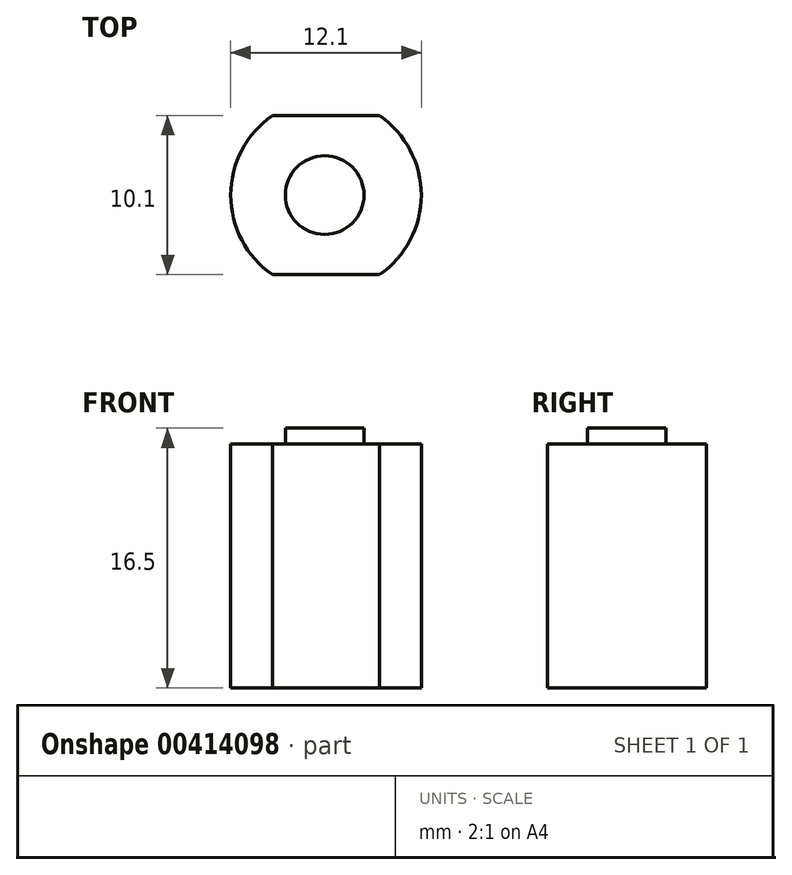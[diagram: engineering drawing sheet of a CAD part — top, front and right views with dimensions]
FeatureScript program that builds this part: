
annotation { "Feature Type Name" : "Feature", "Feature Type Description" : "" }
export const myFeature = defineFeature(function(context is Context, id is Id, definition is map)
    precondition{}
    {
        {
            var Q0;
            Q0=qCreatedBy(makeId("Top.planeOp"),FACE);
            var sketch = newSketch(context, id + "F0", { "sketchPlane" : qUnion([Q0])});
            skLineSegment(sketch, "E0.bottom", {"start": v(3.4, 5.05) * mm, "end": v(-3.4, 5.05) * mm});
            skLineSegment(sketch, "E0.top", {"start": v(3.4, -5.05) * mm, "end": v(-3.4, -5.05) * mm});
            skPoint(sketch, "E0.middle", {"position": v(0, 0) * mm});
            skPoint(sketch, "E1", {"position": v(6.05, 0) * mm});
            skPoint(sketch, "E2", {"position": v(-6.05, 0) * mm});
            skArc(sketch, "E3", {"start": v(3.4, -5.05) * mm, "mid": v(6.05, 0) * mm, "end": v(3.4, 5.05) * mm});
            skArc(sketch, "E4", {"start": v(-3.4, 5.05) * mm, "mid": v(-6.05, 0) * mm, "end": v(-3.4, -5.05) * mm});
            skPoint(sketch, "E5.orphan", {"position": v(6.05, 5.05) * mm});
            skPoint(sketch, "E0.left.end.orphan", {"position": v(6.05, -5.05) * mm});
            skPoint(sketch, "E6.orphan", {"position": v(-6.05, -5.05) * mm});
            skPoint(sketch, "E7.orphan", {"position": v(-6.05, 5.05) * mm});
            skSolve(sketch);
        }
        {
            var Q0;
            Q0=makeQuery(id+"F0.imprint","IMPRINT",FACE,{"disambiguationData":[TD([[makeQuery(id+"F0.imprint","IMPRINT",EDGE,{"derivedFrom":sQuery(id+"F0.wireOp",EDGE,"E0.bottom")}),1.0]])]});
            extrude(context, id + "F1", {"entities" : qUnion([Q0]), "depth" : 15.5 * mm});
        }
        {
            var Q0;
            Q0=makeQuery(id+"F1.opExtrude","CAP_FACE",FACE,{"disambiguationData":[OSD([sQuery(id+"F0.wireOp",EDGE,"E0.bottom"),sQuery(id+"F0.wireOp",EDGE,"E0.top"),sQuery(id+"F0.wireOp",EDGE,"E3"),sQuery(id+"F0.wireOp",EDGE,"E4")])],"isStart":false});
            var sketch = newSketch(context, id + "F2", { "sketchPlane" : qUnion([Q0])});
            skCircle(sketch, "E8", {"center": v(-0.09, 0) * mm, "radius": 2.5 * mm});
            skLineSegment(sketch, "E9.trimOffspring", {"start": v(-0.09, 0) * mm, "end": v(0, 0) * mm});
            skPoint(sketch, "E10.trimOffspring.end.orphan", {"position": v(0, -5.05) * mm});
            skPoint(sketch, "E11.start.orphan", {"position": v(-6.05, 0) * mm});
            skPoint(sketch, "E12.start.orphan", {"position": v(0, 5.05) * mm});
            skPoint(sketch, "E13.trimOffspring.end.orphan", {"position": v(6.05, 0) * mm});
            skSolve(sketch);
        }
        {
            var Q0;
            Q0=makeQuery(id+"F2.imprint","IMPRINT",FACE,{"disambiguationData":[TD([[makeQuery(id+"F2.imprint","IMPRINT",EDGE,{"derivedFrom":sQuery(id+"F2.wireOp",EDGE,"E8")}),1.0]])]});
            extrude(context, id + "F3", {"entities" : qUnion([Q0]), "operationType" : NewBodyOperationType.ADD, "depth" : 1 * mm});
        }
    });
